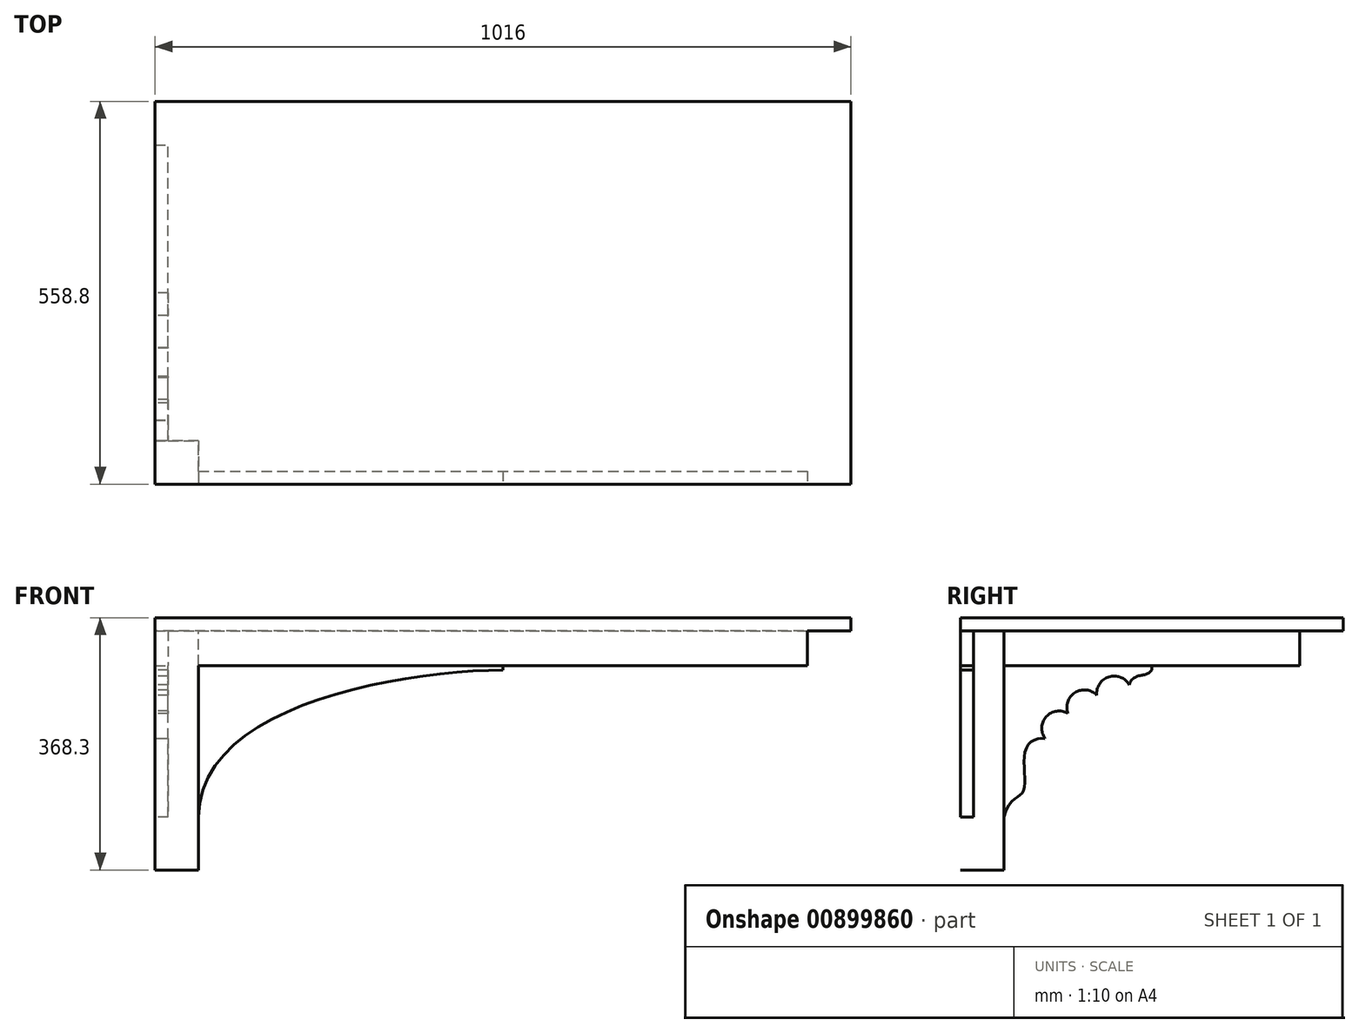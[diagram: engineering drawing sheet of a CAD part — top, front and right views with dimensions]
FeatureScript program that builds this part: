
annotation { "Feature Type Name" : "Feature", "Feature Type Description" : "" }
export const myFeature = defineFeature(function(context is Context, id is Id, definition is map)
    precondition{}
    {
        {
            var Q0;
            Q0=qCreatedBy(makeId("Top.planeOp"),FACE);
            cPlane(context, id + "F0", {"entities" : qUnion([Q0]), "cplaneType" : CPlaneType.OFFSET, "offset" : 368.3 * mm, "width" : 152.4 * mm, "height" : 152.4 * mm});
        }
        {
            var Q0;
            Q0=qCreatedBy(id+"F0.planeOp",FACE);
            var sketch = newSketch(context, id + "F1", { "sketchPlane" : qUnion([Q0])});
            skLineSegment(sketch, "E0.bottom", {"start": v(508, 279.4) * mm, "end": v(-508, 279.4) * mm});
            skLineSegment(sketch, "E0.top", {"start": v(508, -279.4) * mm, "end": v(-508, -279.4) * mm});
            skLineSegment(sketch, "E0.left", {"start": v(508, 279.4) * mm, "end": v(508, -279.4) * mm});
            skLineSegment(sketch, "E0.right", {"start": v(-508, 279.4) * mm, "end": v(-508, -279.4) * mm});
            skPoint(sketch, "E0.middle", {"position": v(0, 0) * mm});
            skSolve(sketch);
        }
        {
            var Q0;
            Q0 = qSketchRegion(id + "F1", true);
            extrude(context, id + "F2", {"entities" : qUnion([Q0]), "oppositeDirection" : true, "depth" : 19.05 * mm, "offsetDistance" : 25.4 * mm});
        }
        {
            var Q0;
            Q0=makeQuery(id+"F2.opExtrude","CAP_FACE",FACE,{"disambiguationData":[OSD([sQuery(id+"F1.wireOp",EDGE,"E0.bottom"),sQuery(id+"F1.wireOp",EDGE,"E0.top"),sQuery(id+"F1.wireOp",EDGE,"E0.left"),sQuery(id+"F1.wireOp",EDGE,"E0.right")])],"isStart":false});
            var sketch = newSketch(context, id + "F3", { "sketchPlane" : qUnion([Q0])});
            skLineSegment(sketch, "E1.bottom", {"start": v(-508, 279.4) * mm, "end": v(-444.5, 279.4) * mm});
            skLineSegment(sketch, "E1.top", {"start": v(-508, 215.9) * mm, "end": v(-444.5, 215.9) * mm});
            skLineSegment(sketch, "E1.left", {"start": v(-508, 279.4) * mm, "end": v(-508, 215.9) * mm});
            skLineSegment(sketch, "E1.right", {"start": v(-444.5, 279.4) * mm, "end": v(-444.5, 215.9) * mm});
            skSolve(sketch);
        }
        {
            var Q0;
            Q0 = qSketchRegion(id + "F3", true);
            var Q1;
            Q1=qCreatedBy(makeId("Top.planeOp"),FACE);
            extrude(context, id + "F4", {"entities" : qUnion([Q0]), "endBound" : BoundingType.UP_TO_SURFACE, "depth" : 25.4 * mm, "endBoundEntityFace" : qUnion([Q1]), "offsetDistance" : 25.4 * mm});
        }
        {
            var Q0;
            Q0=qCreatedBy(makeId("Right.planeOp"),FACE);
            var sketch = newSketch(context, id + "F5", { "sketchPlane" : qUnion([Q0])});
            skLineSegment(sketch, "E2.bottom", {"start": v(-279.4, 349.25) * mm, "end": v(-260.35, 349.25) * mm});
            skLineSegment(sketch, "E2.top", {"start": v(-279.4, 298.45) * mm, "end": v(-260.35, 298.45) * mm});
            skLineSegment(sketch, "E2.left", {"start": v(-279.4, 349.25) * mm, "end": v(-279.4, 298.45) * mm});
            skLineSegment(sketch, "E2.right", {"start": v(-260.35, 349.25) * mm, "end": v(-260.35, 298.45) * mm});
            skSolve(sketch);
        }
        {
            var Q0;
            Q0 = qSketchRegion(id + "F5", true);
            extrude(context, id + "F6", {"entities" : qUnion([Q0]), "endBound" : BoundingType.UP_TO_NEXT, "oppositeDirection" : true, "depth" : 25.4 * mm, "offsetDistance" : 25.4 * mm});
        }
        {
            var Q0;
            Q0=makeQuery(id+"F6.opExtrude","SWEPT_BODY",BODY,{"disambiguationData":[OSD([sQuery(id+"F5.wireOp",EDGE,"E2.bottom"),sQuery(id+"F5.wireOp",EDGE,"E2.top"),sQuery(id+"F5.wireOp",EDGE,"E2.left"),sQuery(id+"F5.wireOp",EDGE,"E2.right")])]});
            var Q1;
            Q1=makeQuery(id+"F6.opExtrude","CAP_FACE",FACE,{"disambiguationData":[OSD([sQuery(id+"F5.wireOp",EDGE,"E2.bottom"),sQuery(id+"F5.wireOp",EDGE,"E2.top"),sQuery(id+"F5.wireOp",EDGE,"E2.left"),sQuery(id+"F5.wireOp",EDGE,"E2.right")])],"isStart":true});
            mirror(context, id + "F7", {"operationType" : NewBodyOperationType.ADD, "entities" : qUnion([Q0]), "mirrorPlane" : qUnion([Q1])});
        }
        {
            var Q0;
            Q0=qCreatedBy(makeId("Front.planeOp"),FACE);
            var sketch = newSketch(context, id + "F8", { "sketchPlane" : qUnion([Q0])});
            skLineSegment(sketch, "E3.bottom", {"start": v(-508, 349.25) * mm, "end": v(-488.95, 349.25) * mm});
            skLineSegment(sketch, "E3.top", {"start": v(-508, 298.45) * mm, "end": v(-488.95, 298.45) * mm});
            skLineSegment(sketch, "E3.left", {"start": v(-508, 349.25) * mm, "end": v(-508, 298.45) * mm});
            skLineSegment(sketch, "E3.right", {"start": v(-488.95, 349.25) * mm, "end": v(-488.95, 298.45) * mm});
            skSolve(sketch);
        }
        {
            var Q0;
            Q0 = qSketchRegion(id + "F8", true);
            extrude(context, id + "F9", {"entities" : qUnion([Q0]), "endBound" : BoundingType.UP_TO_NEXT, "depth" : 25.4 * mm, "offsetDistance" : 25.4 * mm});
        }
        {
            var Q0;
            Q0=makeQuery(id+"F9.opExtrude","SWEPT_BODY",BODY,{"disambiguationData":[OSD([sQuery(id+"F8.wireOp",EDGE,"E3.bottom"),sQuery(id+"F8.wireOp",EDGE,"E3.top"),sQuery(id+"F8.wireOp",EDGE,"E3.left"),sQuery(id+"F8.wireOp",EDGE,"E3.right")])]});
            var Q1;
            Q1=makeQuery(id+"F9.opExtrude","CAP_FACE",FACE,{"disambiguationData":[OSD([sQuery(id+"F8.wireOp",EDGE,"E3.bottom"),sQuery(id+"F8.wireOp",EDGE,"E3.top"),sQuery(id+"F8.wireOp",EDGE,"E3.left"),sQuery(id+"F8.wireOp",EDGE,"E3.right")])],"isStart":true});
            mirror(context, id + "F10", {"operationType" : NewBodyOperationType.ADD, "entities" : qUnion([Q0]), "mirrorPlane" : qUnion([Q1])});
        }
        {
            var Q0;
            {var subQ0=makeQuery(id+"F9.opExtrude","SWEPT_FACE",FACE,{"disambiguationData":[OSD([sQuery(id+"F8.wireOp",EDGE,"E3.left")])]});Q0=makeQuery(id+"F10.boolean.opBoolean","MERGE",FACE,{"derivedFrom":[subQ0,makeQuery(id+"F10.opPattern","COPY",FACE,{"derivedFrom":subQ0,"instanceName":"1"})]});}
            var sketch = newSketch(context, id + "F11", { "sketchPlane" : qUnion([Q0])});
            skLineSegment(sketch, "E4", {"start": v(0, 298.45) * mm, "end": v(0, 0) * mm, "construction": true});
            skFitSpline(sketch, "E5", {"points": [v(731.55, 406.27) * mm, v(746.54, 395.44) * mm, v(763.39, 386.1) * mm], "startDerivative": vector(27.4, -49.12) * mm, "endDerivative": vector(37.33, -48.88) * mm});
            skArc(sketch, "E6", {"start": v(814.4, 371.65) * mm, "mid": v(791.33, 387.49) * mm, "end": v(763.39, 386.1) * mm});
            skArc(sketch, "E7", {"start": v(858.9, 342.6) * mm, "mid": v(841.86, 365.12) * mm, "end": v(814.4, 371.65) * mm});
            skArc(sketch, "E8", {"start": v(887.62, 301.23) * mm, "mid": v(880.46, 326.92) * mm, "end": v(858.9, 342.6) * mm});
            skFitSpline(sketch, "E9", {"points": [v(887.62, 301.23) * mm, v(899.26, 278.45) * mm, v(893, 236.4) * mm, v(897.28, 232.18) * mm], "startDerivative": vector(46.82, -26.7) * mm, "endDerivative": vector(30.1, -4.16) * mm});
            skFitSpline(sketch, "E10", {"points": [v(897.28, 232.18) * mm, v(897.28, 229.45) * mm, v(905.42, 215.97) * mm], "startDerivative": vector(-1.62, -7.94) * mm, "endDerivative": vector(17.84, -24.91) * mm});
            skArc(sketch, "E11", {"start": v(887.62, 301.23) * mm, "mid": v(836.35, 359.55) * mm, "end": v(763.39, 386.1) * mm});
            skLineSegment(sketch, "E12", {"start": v(731.55, 406.27) * mm, "end": v(731.55, 216.95) * mm});
            skLineSegment(sketch, "E13", {"start": v(731.55, 216.95) * mm, "end": v(930.56, 216.95) * mm});
            skArc(sketch, "E14", {"start": v(0, 273.05) * mm, "mid": v(134.7, 217.25) * mm, "end": v(190.5, 82.55) * mm, "construction": true});
            skLineSegment(sketch, "E15", {"start": v(0, 82.55) * mm, "end": v(190.5, 82.55) * mm, "construction": true});
            skLineSegment(sketch, "E16", {"start": v(0, 82.55) * mm, "end": v(33.08, 270.16) * mm, "construction": true});
            skLineSegment(sketch, "E17", {"start": v(0, 82.55) * mm, "end": v(80.5, 255.2) * mm, "construction": true});
            skLineSegment(sketch, "E18", {"start": v(0, 82.55) * mm, "end": v(122.45, 228.48) * mm, "construction": true});
            skLineSegment(sketch, "E19", {"start": v(0, 82.55) * mm, "end": v(156.05, 191.82) * mm, "construction": true});
            skArc(sketch, "E20", {"start": v(80.5, 255.2) * mm, "mid": v(62.87, 281.96) * mm, "end": v(33.08, 270.16) * mm});
            skArc(sketch, "E21", {"start": v(122.45, 228.48) * mm, "mid": v(112.34, 258.9) * mm, "end": v(80.5, 255.2) * mm});
            skArc(sketch, "E22", {"start": v(156.05, 191.82) * mm, "mid": v(154.15, 223.8) * mm, "end": v(122.45, 228.48) * mm});
            skFitSpline(sketch, "E23", {"points": [v(0, 292.06) * mm, v(14.97, 284.37) * mm, v(33.08, 270.16) * mm], "startDerivative": vector(42, -47.9) * mm, "endDerivative": vector(10.16, -53.94) * mm});
            skLineSegment(sketch, "E24", {"start": v(0, 292.06) * mm, "end": v(0, 298.45) * mm});
            skLineSegment(sketch, "E25", {"start": v(0, 298.45) * mm, "end": v(215.9, 298.45) * mm});
            skLineSegment(sketch, "E26", {"start": v(215.9, 298.45) * mm, "end": v(215.9, 76.93) * mm});
            skFitSpline(sketch, "E27", {"points": [v(156.05, 191.82) * mm, v(184.3, 175.55) * mm, v(187.7, 115.1) * mm, v(215.9, 76.93) * mm], "startDerivative": vector(125.29, 24.4) * mm, "endDerivative": vector(64.67, -272.67) * mm});
            skSolve(sketch);
        }
        {
            var Q0;
            Q0=makeQuery(id+"F11.imprint","IMPRINT",FACE,{"disambiguationData":[TD([[makeQuery(id+"F11.imprint","IMPRINT",EDGE,{"derivedFrom":sQuery(id+"F11.wireOp",EDGE,"E20")}),-1.0]])]});
            extrude(context, id + "F12", {"entities" : qUnion([Q0]), "oppositeDirection" : true, "depth" : 19.05 * mm, "offsetDistance" : 25.4 * mm});
        }
        {
            var Q0;
            Q0=makeQuery(id+"F4.opExtrude","SWEPT_FACE",FACE,{"disambiguationData":[OSD([sQuery(id+"F3.wireOp",EDGE,"E1.bottom")])]});
            var sketch = newSketch(context, id + "F13", { "sketchPlane" : qUnion([Q0])});
            skLineSegment(sketch, "E28", {"start": v(0, 0) * mm, "end": v(0, 298.45) * mm, "construction": true});
            skFitSpline(sketch, "E29", {"points": [v(-444.5, 76.94) * mm, v(0, 292.07) * mm], "startDerivative": vector(0, 487.28) * mm, "endDerivative": vector(472.18, 6.48) * mm});
            skLineSegment(sketch, "E30", {"start": v(0, 292.07) * mm, "end": v(0, 298.45) * mm});
            skLineSegment(sketch, "E31", {"start": v(-444.5, 76.94) * mm, "end": v(-444.5, 298.45) * mm});
            skLineSegment(sketch, "E32", {"start": v(-444.5, 298.45) * mm, "end": v(0, 298.45) * mm});
            skSolve(sketch);
        }
        {
            var Q0;
            Q0 = qSketchRegion(id + "F13", true);
            extrude(context, id + "F14", {"entities" : qUnion([Q0]), "oppositeDirection" : true, "depth" : 19.05 * mm, "offsetDistance" : 25.4 * mm});
        }
    });
